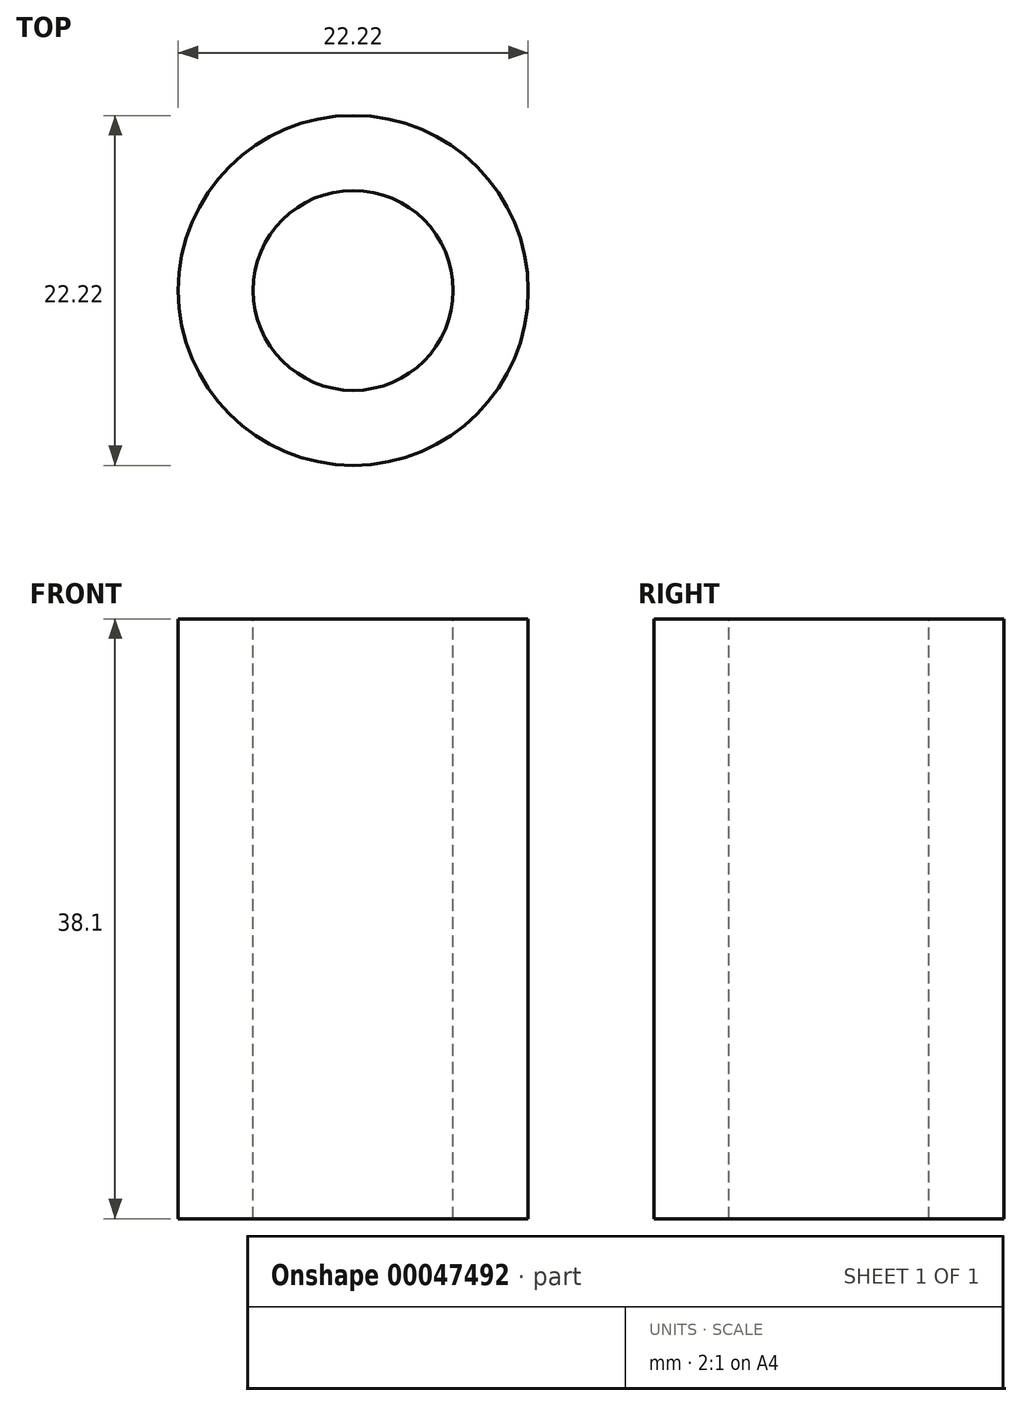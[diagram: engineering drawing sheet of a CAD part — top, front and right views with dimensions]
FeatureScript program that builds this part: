
annotation { "Feature Type Name" : "Feature", "Feature Type Description" : "" }
export const myFeature = defineFeature(function(context is Context, id is Id, definition is map)
    precondition{}
    {
        {
            var Q0;
            Q0=qCreatedBy(makeId("Top.planeOp"),FACE);
            var sketch = newSketch(context, id + "F0", { "sketchPlane" : qUnion([Q0])});
            skCircle(sketch, "E0", {"center": v(0, 0) * mm, "radius": 11.11 * mm});
            skSolve(sketch);
        }
        {
            var Q0;
            Q0 = qSketchRegion(id + "F0", true);
            extrude(context, id + "F1", {"entities" : qUnion([Q0]), "depth" : 38.1 * mm, "symmetric" : true});
        }
        {
            var Q0;
            Q0=makeQuery(id+"F1.opExtrude","CAP_FACE",FACE,{"disambiguationData":[OSD([sQuery(id+"F0.wireOp",EDGE,"E0")])],"isStart":false});
            var sketch = newSketch(context, id + "F2", { "sketchPlane" : qUnion([Q0])});
            skCircle(sketch, "E1", {"center": v(0, 0) * mm, "radius": 6.35 * mm});
            skSolve(sketch);
        }
        {
            var Q0;
            Q0 = qSketchRegion(id + "F2", true);
            extrude(context, id + "F3", {"entities" : qUnion([Q0]), "operationType" : NewBodyOperationType.REMOVE, "endBound" : BoundingType.THROUGH_ALL, "oppositeDirection" : true, "depth" : 25.4 * mm});
        }
    });
